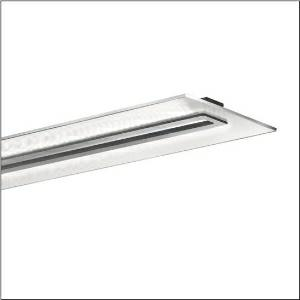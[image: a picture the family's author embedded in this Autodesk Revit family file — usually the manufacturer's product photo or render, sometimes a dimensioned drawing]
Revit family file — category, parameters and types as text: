
# Revit family: vega_r__11_5mn238dle0s3_873d
name_source: partatom
category: Lighting Fixtures
units: mm (PartAtom-declared; Revit-internal decimal feet)

## family parameters
Cut with Voids When Loaded = No
Host = Face
Light Source = No
Part Type = Normal
Room Calculation Point = No
Round Connector Dimension = Use Diameter
Shared = No

## types (1)
- --- (1 x LED 3000K / CRI = 80 (unbekannt), 7300 lm, 3000K)
    Apparent Load = 62 VA
    CIE Flux Codes = 61 86 97 62 100
    Color Rendering = 80
    Color Temperature = 3000K
    Default Elevation = 1800 mm
    Description = Vega® 11, office luminaire, primary light control with prismatic reflector, of PMMA, transparent prismatic structure, CAT 2 (L<= 1500cd/m²), light emission: direct/indirect distribution, primary light characteristic: symmetric, installation type: suspended mounting, surface-mounted, LED rated luminous flux: 7.300 lm, light colour: 830, colour temperature: 3000K, control gear: ECG, with terminal, 3+2-pole, max. 2.5mm², mains connection: 230V, AC, 50Hz, connection cable inclusive, cable length: 1,5 m, rated input power: 62W, luminaire housing, rectangular, rounded, of aluminium section, anodised, metallic grey (RAL 9006), length: 1.250 mm, width: 350 mm, height: 43mm, luminaire housing, lower part, of aluminium section, anodised, metallic grey (RAL 9006), of PC, grey, protection rating (complete): IP20, insulation class (complete): insulation class I (protective earthing), certification: CE, permissible ambient temperature for indoor applications: 0..+35°C, standard: EN 50419, packaging unit: 1 piece
    Height = 40 mm  [stored 0.131234 ft]
    Lamp = 1 x LED 3000K / CRI >= 80 (unbekannt)
    Lamp Light Flux = 7300 lm
    Lamp count = 1
    Length = 1250 mm
    Luminous efficacy = 118 lm/W
    Manufacturer = Siteco
    ModVariant = No
    Model = 5MN238DLE0S3
    Mounting Place = Ceiling
    Mounting Type = Pendant
    Number of Poles = 1
    OnlyDefault = Yes
    Power Factor = 1
    Product Name = Vega® 11
    Product group = office luminaire | ceiling pendant
    ProductGroupID = 905
    Protection Class = Protection class I
    Protection Degree = IP 20
    RLX_Detail_Level = 1
    RlxData = <blob elided: 62837 chars, md5=c337d83e>
    Socket = socket
    Standby Power = 0 W
    System Light Flux = 7300 lm
    System Power = 62 W
    Type Comments = factory setting: luminous flux: 100 % | dim-lin: 254 | 460 mA
    Type Image = l_1004807.jpg
    URL = http://relux.com
    VarID = @adj_147169
    Voltage = 0 V
    Weight = 0.00 kg
    Width = 350 mm

note: [stored X ft] marks values corroborated as IEEE doubles in the binary element streams (Revit-internal decimal feet)

## geometry (parser evidence)
native form markers: Blend x4, Sweep x14
no freeform markers — native parametric forms only
